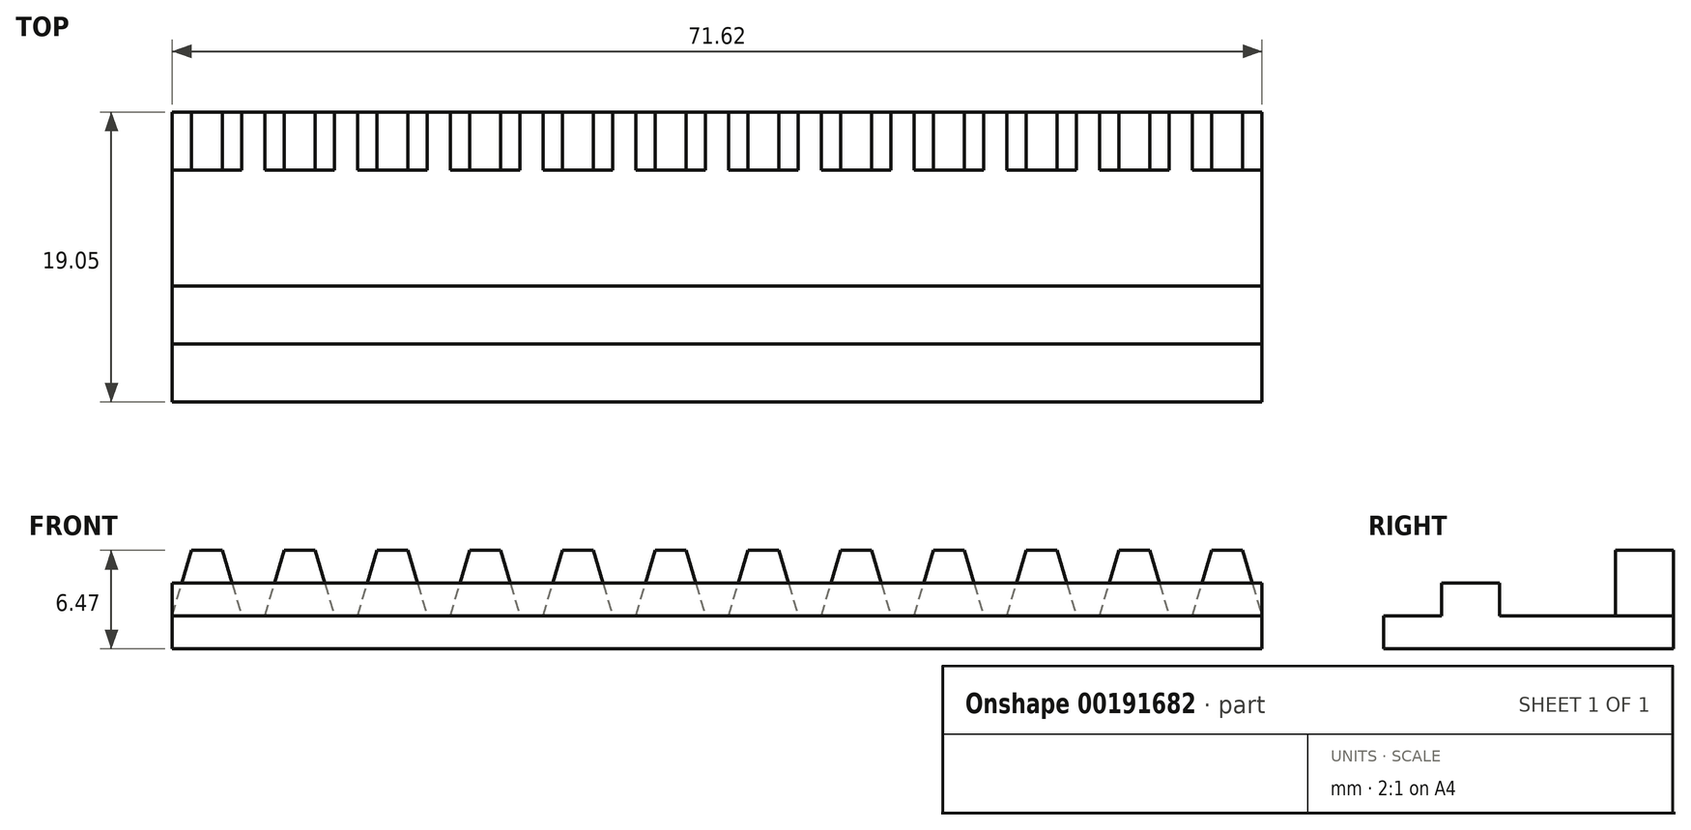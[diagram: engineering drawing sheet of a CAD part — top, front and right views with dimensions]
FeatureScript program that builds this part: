
annotation { "Feature Type Name" : "Feature", "Feature Type Description" : "" }
export const myFeature = defineFeature(function(context is Context, id is Id, definition is map)
    precondition{}
    {
        {
            var Q0;
            Q0=qCreatedBy(makeId("Front.planeOp"),FACE);
            var sketch = newSketch(context, id + "F0", { "sketchPlane" : qUnion([Q0])});
            skLineSegment(sketch, "E0.bottom", {"start": v(-38.44, 14.74) * mm, "end": v(33.18, 14.74) * mm});
            skLineSegment(sketch, "E0.top", {"start": v(-38.44, 16.9) * mm, "end": v(33.18, 16.9) * mm});
            skLineSegment(sketch, "E0.left", {"start": v(-38.44, 14.74) * mm, "end": v(-38.44, 16.9) * mm});
            skLineSegment(sketch, "E1", {"start": v(-38.44, 16.9) * mm, "end": v(-37.17, 21.21) * mm});
            skLineSegment(sketch, "E2", {"start": v(-37.17, 21.21) * mm, "end": v(-35.14, 21.21) * mm});
            skLineSegment(sketch, "E3", {"start": v(-35.14, 21.21) * mm, "end": v(-33.87, 16.9) * mm});
            skLineSegment(sketch, "E4", {"start": v(-38.44, 16.9) * mm, "end": v(-33.87, 16.9) * mm});
            skLineSegment(sketch, "E5", {"start": v(-36.16, 21.21) * mm, "end": v(-36.16, 16.9) * mm, "construction": true});
            skLineSegment(sketch, "E6", {"start": v(33.18, 14.74) * mm, "end": v(33.18, 16.9) * mm});
            skLineSegment(sketch, "E7.1.0.0", {"start": v(-29.05, 21.21) * mm, "end": v(-27.78, 16.9) * mm});
            skLineSegment(sketch, "E7.1.0.1", {"start": v(-32.35, 16.9) * mm, "end": v(-31.08, 21.21) * mm});
            skLineSegment(sketch, "E7.1.0.2", {"start": v(-31.08, 21.21) * mm, "end": v(-29.05, 21.21) * mm});
            skLineSegment(sketch, "E7.2.0.0", {"start": v(-22.95, 21.21) * mm, "end": v(-21.68, 16.9) * mm});
            skLineSegment(sketch, "E7.2.0.1", {"start": v(-26.25, 16.9) * mm, "end": v(-24.98, 21.21) * mm});
            skLineSegment(sketch, "E7.2.0.2", {"start": v(-24.98, 21.21) * mm, "end": v(-22.95, 21.21) * mm});
            skLineSegment(sketch, "E7.3.0.0", {"start": v(-16.85, 21.21) * mm, "end": v(-15.58, 16.9) * mm});
            skLineSegment(sketch, "E7.3.0.1", {"start": v(-20.16, 16.9) * mm, "end": v(-18.89, 21.21) * mm});
            skLineSegment(sketch, "E7.3.0.2", {"start": v(-18.89, 21.21) * mm, "end": v(-16.85, 21.21) * mm});
            skLineSegment(sketch, "E7.4.0.0", {"start": v(-10.76, 21.21) * mm, "end": v(-9.49, 16.9) * mm});
            skLineSegment(sketch, "E7.4.0.1", {"start": v(-14.06, 16.9) * mm, "end": v(-12.8, 21.21) * mm});
            skLineSegment(sketch, "E7.4.0.2", {"start": v(-12.8, 21.21) * mm, "end": v(-10.76, 21.21) * mm});
            skLineSegment(sketch, "E7.5.0.0", {"start": v(-4.66, 21.21) * mm, "end": v(-3.4, 16.9) * mm});
            skLineSegment(sketch, "E7.5.0.1", {"start": v(-7.96, 16.9) * mm, "end": v(-6.7, 21.21) * mm});
            skLineSegment(sketch, "E7.5.0.2", {"start": v(-6.7, 21.21) * mm, "end": v(-4.66, 21.21) * mm});
            skLineSegment(sketch, "E7.6.0.0", {"start": v(1.43, 21.21) * mm, "end": v(2.7, 16.9) * mm});
            skLineSegment(sketch, "E7.6.0.1", {"start": v(-1.87, 16.9) * mm, "end": v(-0.6, 21.21) * mm});
            skLineSegment(sketch, "E7.6.0.2", {"start": v(-0.6, 21.21) * mm, "end": v(1.43, 21.21) * mm});
            skLineSegment(sketch, "E7.7.0.0", {"start": v(7.53, 21.21) * mm, "end": v(8.8, 16.9) * mm});
            skLineSegment(sketch, "E7.7.0.1", {"start": v(4.23, 16.9) * mm, "end": v(5.5, 21.21) * mm});
            skLineSegment(sketch, "E7.7.0.2", {"start": v(5.5, 21.21) * mm, "end": v(7.53, 21.21) * mm});
            skLineSegment(sketch, "E7.8.0.0", {"start": v(13.63, 21.21) * mm, "end": v(14.9, 16.9) * mm});
            skLineSegment(sketch, "E7.8.0.1", {"start": v(10.32, 16.9) * mm, "end": v(11.6, 21.21) * mm});
            skLineSegment(sketch, "E7.8.0.2", {"start": v(11.6, 21.21) * mm, "end": v(13.63, 21.21) * mm});
            skLineSegment(sketch, "E7.9.0.0", {"start": v(19.72, 21.21) * mm, "end": v(21, 16.9) * mm});
            skLineSegment(sketch, "E7.9.0.1", {"start": v(16.42, 16.9) * mm, "end": v(17.69, 21.21) * mm});
            skLineSegment(sketch, "E7.9.0.2", {"start": v(17.69, 21.21) * mm, "end": v(19.72, 21.21) * mm});
            skLineSegment(sketch, "E7.10.0.0", {"start": v(25.82, 21.21) * mm, "end": v(27.09, 16.9) * mm});
            skLineSegment(sketch, "E7.10.0.1", {"start": v(22.52, 16.9) * mm, "end": v(23.79, 21.21) * mm});
            skLineSegment(sketch, "E7.10.0.2", {"start": v(23.79, 21.21) * mm, "end": v(25.82, 21.21) * mm});
            skLineSegment(sketch, "E7.11.0.0", {"start": v(31.91, 21.21) * mm, "end": v(33.18, 16.9) * mm});
            skLineSegment(sketch, "E7.11.0.1", {"start": v(28.61, 16.9) * mm, "end": v(29.88, 21.21) * mm});
            skLineSegment(sketch, "E7.11.0.2", {"start": v(29.88, 21.21) * mm, "end": v(31.91, 21.21) * mm});
            skLineSegment(sketch, "E7.direction1", {"start": v(-38.44, 16.9) * mm, "end": v(-32.35, 16.9) * mm, "construction": true});
            skPoint(sketch, "E8.centerSnap0", {"position": v(-38.44, 15.82) * mm});
            skSolve(sketch);
        }
        {
            var Q0;
            Q0=qSketchRegion(id+"F0",true);
            extrude(context, id + "F1", {"entities" : qUnion([Q0]), "depth" : 3.8 * mm});
        }
        {
            var Q0;
            Q0=qCreatedBy(makeId("Right.planeOp"),FACE);
            var Q1;
            Q1=makeQuery(id+"F1.opExtrude","CAP_VERTEX",VERTEX,{"disambiguationData":[OSD([sQuery(id+"F0.wireOp",EDGE,"E0.bottom"),sQuery(id+"F0.wireOp",EDGE,"E6")])],"isStart":false});
            cPlane(context, id + "F2", {"entities" : qUnion([Q0, Q1]), "cplaneType" : CPlaneType.PLANE_POINT, "offset" : 25.4 * mm, "width" : 152.4 * mm, "height" : 152.4 * mm});
        }
        {
            var Q0;
            Q0=qCreatedBy(id+"F2.planeOp",FACE);
            var sketch = newSketch(context, id + "F3", { "sketchPlane" : qUnion([Q0])});
            skLineSegment(sketch, "E9.0", {"start": v(-3.81, 14.74) * mm, "end": v(-3.81, 16.9) * mm});
            skLineSegment(sketch, "E10", {"start": v(-19.05, 16.9) * mm, "end": v(-15.24, 16.9) * mm});
            skLineSegment(sketch, "E11", {"start": v(-11.43, 16.9) * mm, "end": v(-11.43, 19.05) * mm});
            skLineSegment(sketch, "E12", {"start": v(-11.43, 19.05) * mm, "end": v(-15.24, 19.05) * mm});
            skLineSegment(sketch, "E13", {"start": v(-15.24, 19.05) * mm, "end": v(-15.24, 16.9) * mm});
            skLineSegment(sketch, "E14.trimOffspring", {"start": v(-11.43, 16.9) * mm, "end": v(-3.81, 16.9) * mm});
            skLineSegment(sketch, "E15", {"start": v(-3.81, 14.74) * mm, "end": v(-19.05, 14.74) * mm});
            skLineSegment(sketch, "E16", {"start": v(-19.05, 14.74) * mm, "end": v(-19.05, 16.9) * mm});
            skSolve(sketch);
        }
        {
            var Q0;
            Q0=qSketchRegion(id+"F3",true);
            var Q1;
            Q1=makeQuery(id+"F1.opExtrude","SWEPT_FACE",FACE,{"disambiguationData":[OSD([sQuery(id+"F0.wireOp",EDGE,"E0.left")])]});
            extrude(context, id + "F4", {"entities" : qUnion([Q0]), "operationType" : NewBodyOperationType.ADD, "endBound" : BoundingType.UP_TO_SURFACE, "oppositeDirection" : true, "endBoundEntityFace" : qUnion([Q1]), "depth" : 33.02 * mm});
        }
    });
